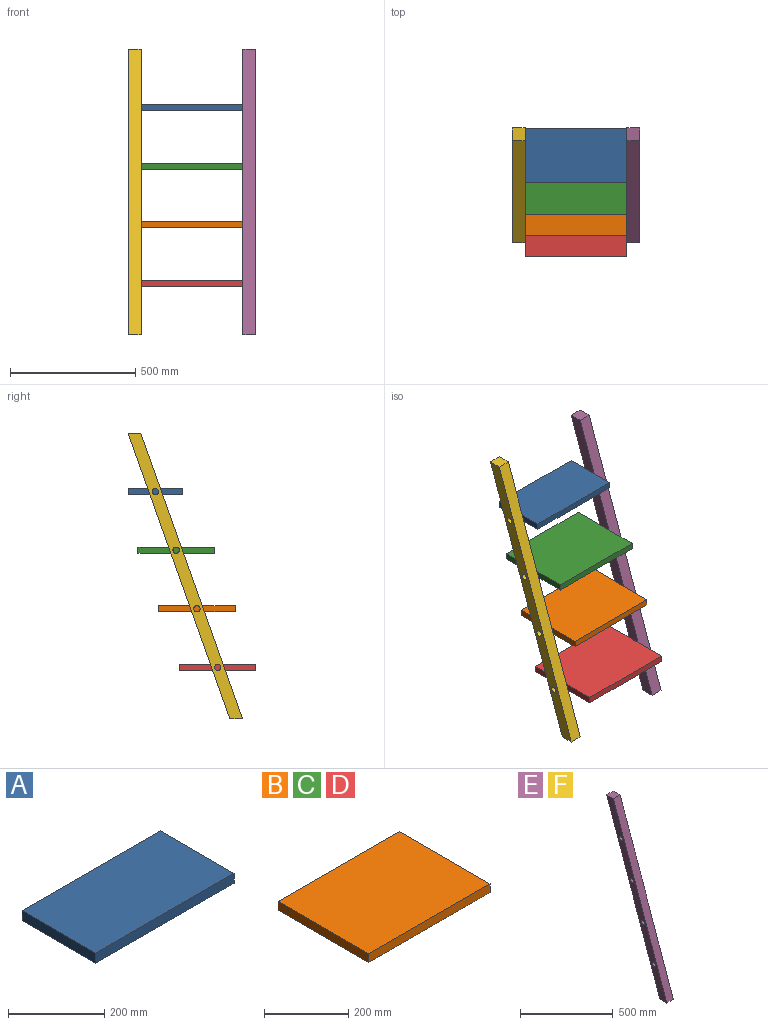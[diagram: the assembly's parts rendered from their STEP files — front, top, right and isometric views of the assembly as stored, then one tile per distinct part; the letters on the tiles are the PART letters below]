
ASSEMBLY  parts=6 mates=4
PART A: 6 faces, bbox 406.4x216.9x25.4 mm
  f0: plane 216.92x25.4mm, normal (1,0,0), area 5509.7mm2, adj f1,f3,f4,f5
  f1: plane 406.4x216.92mm, normal (0,0,1), area 88154.7mm2, adj f0,f2,f4,f5
  f2: plane 216.92x25.4mm, normal (-1,0,0), area 5509.7mm2, adj f1,f3,f4,f5
  f3: plane 406.4x216.92mm, normal (0,0,-1), area 88154.7mm2, adj f0,f2,f4,f5
  f4: plane 406.4x25.4mm, normal (0,-1,0), area 10322.6mm2, adj f0,f1,f2,f3
  f5: plane 406.4x25.4mm, normal (0,1,0), area 10322.6mm2, adj f0,f1,f2,f3
PART B: 6 faces, bbox 406.4x304.8x25.4 mm
  f0: plane 304.8x25.4mm, normal (1,0,0), area 7741.9mm2, adj f1,f3,f4,f5
  f1: plane 406.4x304.8mm, normal (0,0,1), area 123870.7mm2, adj f0,f2,f4,f5
  f2: plane 304.8x25.4mm, normal (-1,0,0), area 7741.9mm2, adj f1,f3,f4,f5
  f3: plane 406.4x304.8mm, normal (0,0,-1), area 123870.7mm2, adj f0,f2,f4,f5
  f4: plane 406.4x25.4mm, normal (0,-1,0), area 10322.6mm2, adj f0,f1,f2,f3
  f5: plane 406.4x25.4mm, normal (0,1,0), area 10322.6mm2, adj f0,f1,f2,f3
PART C: same geometry as B
PART D: same geometry as B
PART E: 10 faces, bbox 50.8x457.2x1143 mm
  f0: plane 1143x406.4mm, normal (0,0.94,-0.34), area 61625.4mm2, adj f1,f3,f8,f9
  f1: plane 50.8x50.8mm, normal (0,0,1), area 2580.6mm2, adj f0,f2,f8,f9
  f2: plane 1143x406.4mm, normal (0,-0.94,0.34), area 61625.4mm2, adj f1,f3,f8,f9
  f3: plane 50.8x50.8mm, normal (0,0,-1), area 2580.6mm2, adj f0,f2,f8,f9
  f4: cylinder r=12.7mm len=50.8mm, axis (-1,0,0), area 4053.7mm2, adj f8,f9
  f5: cylinder r=12.7mm len=50.8mm, axis (-1,0,0), area 4053.7mm2, adj f8,f9
  f6: cylinder r=12.7mm len=50.8mm, axis (-1,0,0), area 4053.7mm2, adj f8,f9
  f7: cylinder r=12.7mm len=50.8mm, axis (-1,0,0), area 4053.7mm2, adj f8,f9
  f8: plane 1143x457.2mm, normal (1,0,0), area 56037.6mm2, adj f0,f1,f2,f3,f4,f5,f6,f7
  f9: plane 1143x457.2mm, normal (-1,0,0), area 56037.6mm2, adj f0,f1,f2,f3,f4,f5,f6,f7
PART F: same geometry as E
PLACE A t=(-30.55,-179.63,281.03)mm
PLACE B t=(-30.55,-302.22,-187.34)mm
PLACE C rot(axis=(0,1,0),180deg) t=(-30.55,-218.95,46.84)mm
PLACE D t=(-30.55,-385.49,-421.53)mm
PLACE E t=(172.65,-1022.41,-55.38)mm
PLACE F t=(-284.55,-1022.41,-55.38)mm
MATE fastened C.f2 <-> E.f5  axis (1,0,0) through (172.65,-371.35,46.84)mm
MATE fastened D.f0 <-> E.f7  axis (1,0,0) through (172.65,-537.89,-421.53)mm
MATE fastened A.f0 <-> E.f4  axis (1,0,0) through (172.65,-288.09,281.03)mm
MATE fastened B.f0 <-> E.f6  axis (1,0,0) through (172.65,-454.62,-187.34)mm
